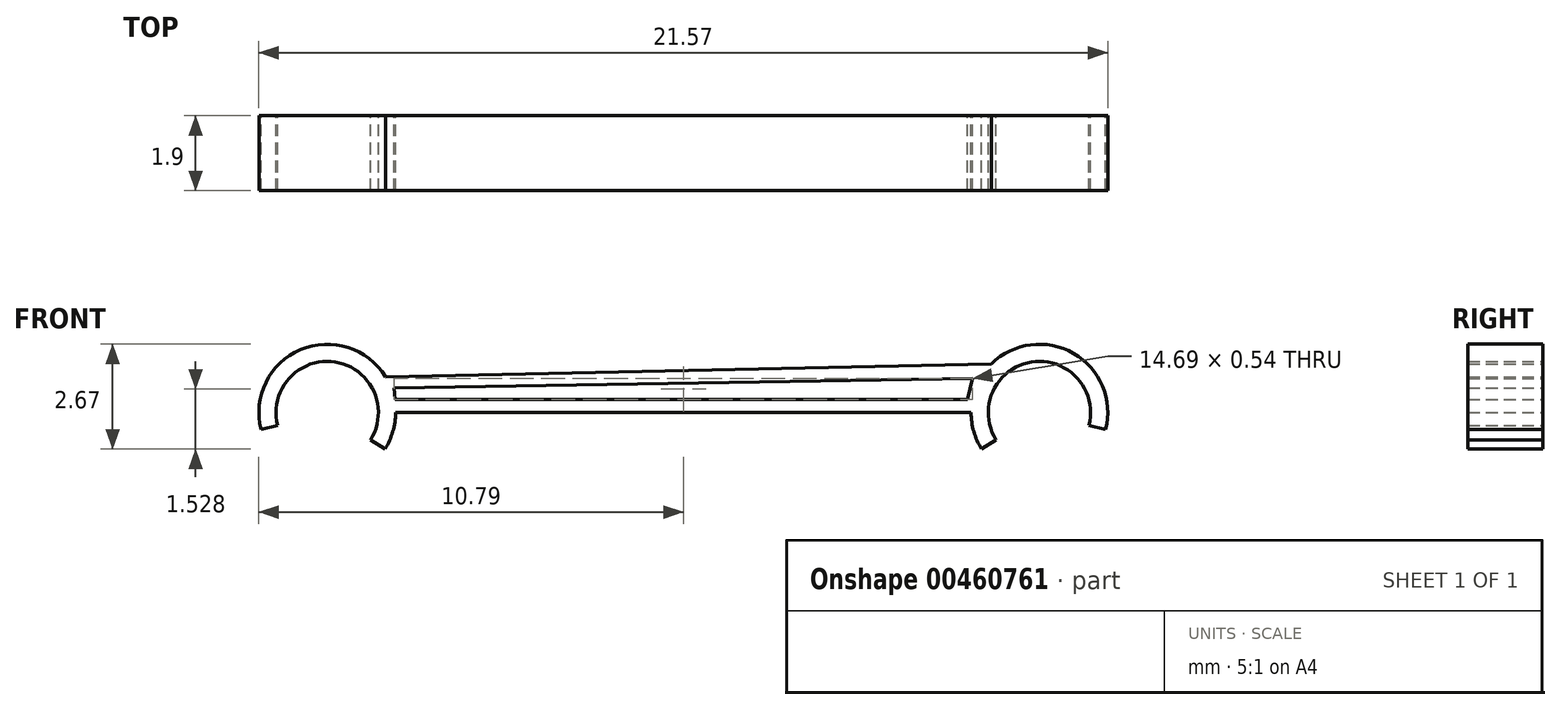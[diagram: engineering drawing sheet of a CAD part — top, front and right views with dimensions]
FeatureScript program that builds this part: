
annotation { "Feature Type Name" : "Feature", "Feature Type Description" : "" }
export const myFeature = defineFeature(function(context is Context, id is Id, definition is map)
    precondition{}
    {
        {
            var Q0;
            Q0=qCreatedBy(makeId("Front.planeOp"),FACE);
            var sketch = newSketch(context, id + "F0", { "sketchPlane" : qUnion([Q0])});
            skArc(sketch, "E0", {"start": v(1.1, -0.7) * mm, "mid": v(0.2, 1.28) * mm, "end": v(-1.26, -0.33) * mm});
            skArc(sketch, "E1", {"start": v(1.47, -0.93) * mm, "mid": v(1.67, -0.48) * mm, "end": v(1.74, 0) * mm});
            skLineSegment(sketch, "E2", {"start": v(-1.26, -0.33) * mm, "end": v(-1.68, -0.43) * mm});
            skLineSegment(sketch, "E3", {"start": v(1.1, -0.7) * mm, "end": v(1.47, -0.93) * mm});
            skLineSegment(sketch, "E4", {"start": v(9.05, 4.2) * mm, "end": v(9.05, -3.1) * mm, "construction": true});
            skLineSegment(sketch, "E5.MirrorCS", {"start": v(19.35, -0.33) * mm, "end": v(19.77, -0.43) * mm});
            skLineSegment(sketch, "E6.MirrorCS", {"start": v(17, -0.7) * mm, "end": v(16.63, -0.93) * mm});
            skArc(sketch, "E7.MirrorCS", {"start": v(17, -0.7) * mm, "mid": v(17.9, 1.28) * mm, "end": v(19.35, -0.33) * mm});
            skArc(sketch, "E8.MirrorCS", {"start": v(16.63, -0.93) * mm, "mid": v(16.43, -0.48) * mm, "end": v(16.36, 0) * mm});
            skLineSegment(sketch, "E9", {"start": v(1.74, 0) * mm, "end": v(16.36, 0) * mm});
            skLineSegment(sketch, "E10", {"start": v(16.88, 1.24) * mm, "end": v(1.48, 0.9) * mm});
            skArc(sketch, "E11.trimOffspring", {"start": v(1.48, 0.9) * mm, "mid": v(-0.68, 1.6) * mm, "end": v(-1.68, -0.43) * mm});
            skPoint(sketch, "E12.orphan", {"position": v(1.56, 0) * mm});
            skArc(sketch, "E13.trimOffspring", {"start": v(16.88, 1.24) * mm, "mid": v(18.96, 1.5) * mm, "end": v(19.77, -0.43) * mm});
            skLineSegment(sketch, "E14", {"start": v(1.7, 0.63) * mm, "end": v(16.4, 0.87) * mm});
            skLineSegment(sketch, "E15", {"start": v(16.4, 0.87) * mm, "end": v(16.27, 0.33) * mm});
            skLineSegment(sketch, "E16", {"start": v(16.27, 0.33) * mm, "end": v(1.73, 0.33) * mm});
            skLineSegment(sketch, "E17", {"start": v(1.73, 0.33) * mm, "end": v(1.7, 0.63) * mm});
            skSolve(sketch);
        }
        {
            var Q0;
            Q0=makeQuery(id+"F0.imprint","IMPRINT",FACE,{"disambiguationData":[TD([[makeQuery(id+"F0.imprint","IMPRINT",EDGE,{"derivedFrom":sQuery(id+"F0.wireOp",EDGE,"E0")}),-1.0]])]});
            extrude(context, id + "F1", {"entities" : qUnion([Q0]), "depth" : 1.9 * mm});
        }
    });
